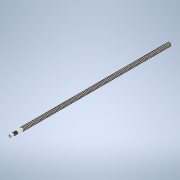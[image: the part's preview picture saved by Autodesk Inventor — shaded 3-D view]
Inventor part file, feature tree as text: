
AUTODESK INVENTOR PART (.ipt)
format: ipt  version: 2020.1 (Build 241239000, 239)  size: 3,923,968 bytes
history: native  units: mm
features: other x2, extrude x1, sketch x1
ambient origin geometry x8: Origin, YZ Plane, XZ Plane, XY Plane, X Axis, Y Axis, Z Axis, Center Point
bodies: Body1 (feature_tree)
feature tree (4):
  other  "Твердое тело1"
  extrude  "Выдавливание1"  Depth=100.0mm TaperAngle=0.0deg
  sketch  "Эскиз1"
  other  "Aesthetic Chamfer"
